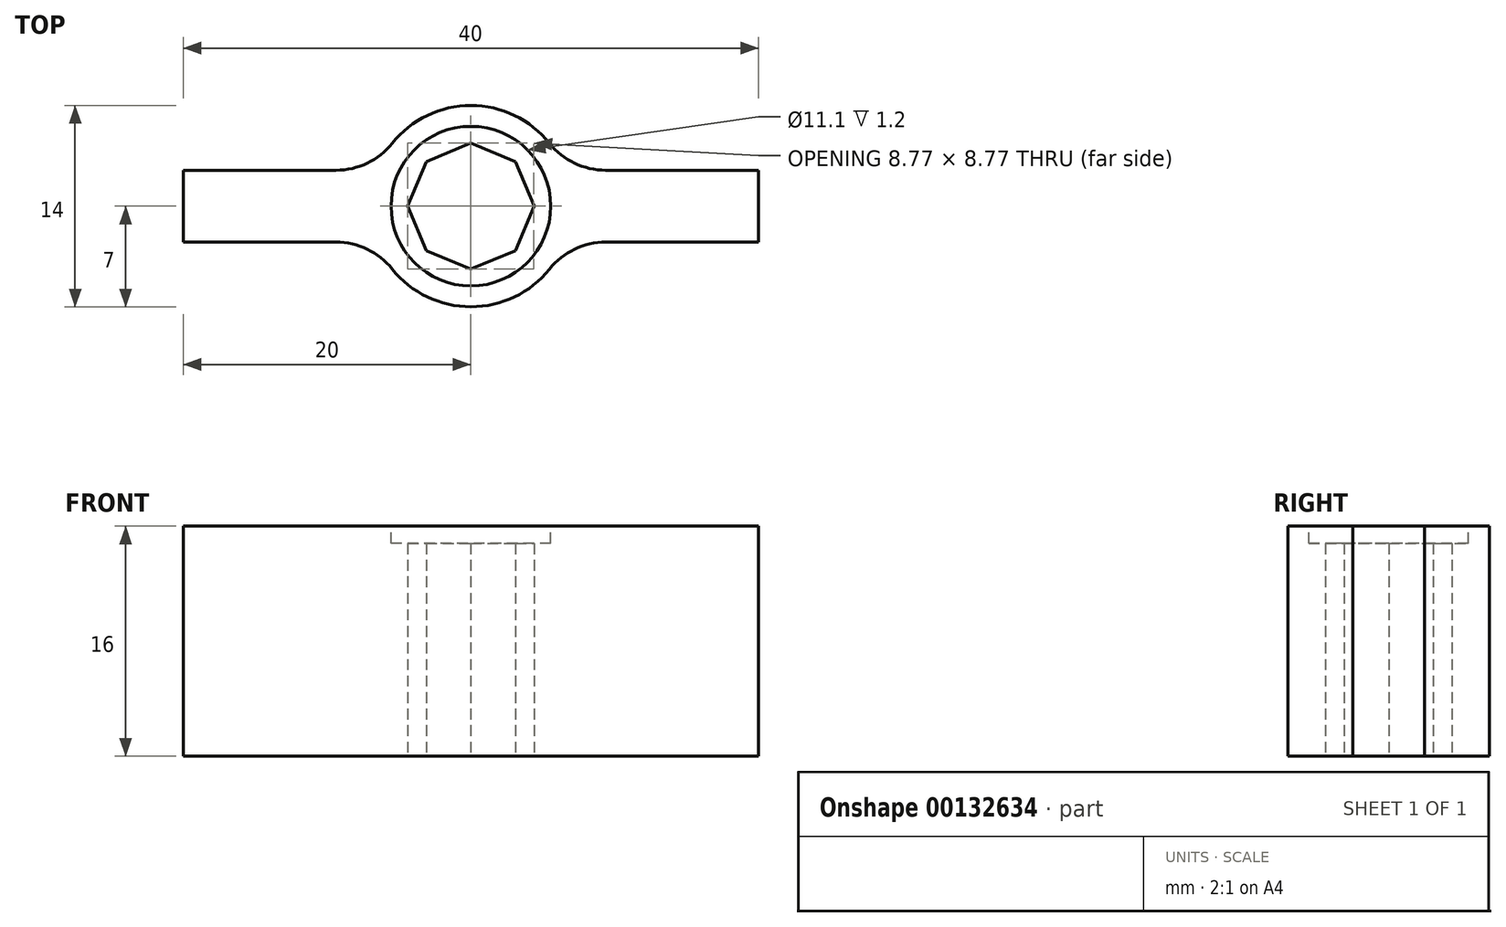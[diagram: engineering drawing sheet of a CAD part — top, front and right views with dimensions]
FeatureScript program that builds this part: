
annotation { "Feature Type Name" : "Feature", "Feature Type Description" : "" }
export const myFeature = defineFeature(function(context is Context, id is Id, definition is map)
    precondition{}
    {
        {
            var Q0;
            Q0=qCreatedBy(makeId("Top.planeOp"),FACE);
            var sketch = newSketch(context, id + "F0", { "sketchPlane" : qUnion([Q0])});
            skCircle(sketch, "E0.cCircle", {"center": v(0, 0) * mm, "radius": 4.05 * mm, "construction": true});
            skLineSegment(sketch, "E0.0", {"start": v(4.38, 0) * mm, "end": v(3.1, -3.1) * mm});
            skLineSegment(sketch, "E0.1", {"start": v(3.1, -3.1) * mm, "end": v(0, -4.38) * mm});
            skLineSegment(sketch, "E0.2", {"start": v(0, -4.38) * mm, "end": v(-3.1, -3.1) * mm});
            skLineSegment(sketch, "E0.3", {"start": v(-3.1, -3.1) * mm, "end": v(-4.38, 0) * mm});
            skLineSegment(sketch, "E0.4", {"start": v(-4.38, 0) * mm, "end": v(-3.1, 3.1) * mm});
            skLineSegment(sketch, "E0.5", {"start": v(-3.1, 3.1) * mm, "end": v(0, 4.38) * mm});
            skLineSegment(sketch, "E0.6", {"start": v(0, 4.38) * mm, "end": v(3.1, 3.1) * mm});
            skLineSegment(sketch, "E0.7", {"start": v(3.1, 3.1) * mm, "end": v(4.38, 0) * mm});
            skPoint(sketch, "E0.0.midPoint", {"position": v(3.74, -1.55) * mm});
            skArc(sketch, "E1", {"start": v(-5.46, -4.37) * mm, "mid": v(0, -7) * mm, "end": v(5.46, -4.37) * mm});
            skLineSegment(sketch, "E2.bottom", {"start": v(20, -2.5) * mm, "end": v(9.37, -2.5) * mm});
            skLineSegment(sketch, "E2.top", {"start": v(20, 2.5) * mm, "end": v(9.37, 2.5) * mm});
            skLineSegment(sketch, "E2.left", {"start": v(20, -2.5) * mm, "end": v(20, 2.5) * mm});
            skLineSegment(sketch, "E2.right", {"start": v(-20, -2.5) * mm, "end": v(-20, 2.5) * mm});
            skLineSegment(sketch, "E3.trimOffspring", {"start": v(-9.37, 2.5) * mm, "end": v(-20, 2.5) * mm});
            skLineSegment(sketch, "E4.trimOffspring", {"start": v(-3.19, 2.5) * mm, "end": v(-3.35, 2.5) * mm});
            skLineSegment(sketch, "E5.trimOffspring", {"start": v(3.35, 2.5) * mm, "end": v(3.19, 2.5) * mm});
            skLineSegment(sketch, "E6.trimOffspring", {"start": v(-3.19, -2.5) * mm, "end": v(-3.35, -2.5) * mm});
            skLineSegment(sketch, "E7.trimOffspring", {"start": v(-9.37, -2.5) * mm, "end": v(-20, -2.5) * mm});
            skArc(sketch, "E8.trimOffspring", {"start": v(5.46, 4.37) * mm, "mid": v(0, 7) * mm, "end": v(-5.46, 4.37) * mm});
            skPoint(sketch, "E9.visualSharp", {"position": v(-6.54, 2.5) * mm});
            skArc(sketch, "E9.filletArc", {"start": v(-9.37, 2.5) * mm, "mid": v(-7.2, 3) * mm, "end": v(-5.46, 4.38) * mm});
            skPoint(sketch, "E10.visualSharp", {"position": v(6.54, 2.5) * mm});
            skArc(sketch, "E10.filletArc", {"start": v(5.46, 4.37) * mm, "mid": v(7.2, 3) * mm, "end": v(9.37, 2.5) * mm});
            skPoint(sketch, "E11.visualSharp", {"position": v(6.54, -2.5) * mm});
            skArc(sketch, "E11.filletArc", {"start": v(9.37, -2.5) * mm, "mid": v(7.2, -3) * mm, "end": v(5.46, -4.37) * mm});
            skPoint(sketch, "E12.visualSharp", {"position": v(-6.54, -2.5) * mm});
            skArc(sketch, "E12.filletArc", {"start": v(-5.46, -4.38) * mm, "mid": v(-7.2, -3) * mm, "end": v(-9.37, -2.5) * mm});
            skSolve(sketch);
        }
        {
            var Q0;
            {var subQ1=sQuery(id+"F0.wireOp",EDGE,"E0.0");Q0=makeQuery(id+"F0.imprint","IMPRINT",FACE,{"disambiguationData":[TD([[makeQuery(id+"F0.imprint","IMPRINT",EDGE,{"derivedFrom":subQ1}),1.0]])]});}
            extrude(context, id + "F1", {"entities" : qUnion([Q0]), "endBound" : BoundingType.SYMMETRIC, "depth" : 16 * mm});
        }
        {
            var Q0;
            Q0=makeQuery(id+"F1.opExtrude","CAP_FACE",FACE,{"disambiguationData":[OSD([sQuery(id+"F0.wireOp",EDGE,"E0.0"),sQuery(id+"F0.wireOp",EDGE,"E0.1"),sQuery(id+"F0.wireOp",EDGE,"E0.2"),sQuery(id+"F0.wireOp",EDGE,"E0.3"),sQuery(id+"F0.wireOp",EDGE,"E0.4"),sQuery(id+"F0.wireOp",EDGE,"E0.5"),sQuery(id+"F0.wireOp",EDGE,"E0.6"),sQuery(id+"F0.wireOp",EDGE,"E0.7"),sQuery(id+"F0.wireOp",EDGE,"E1"),sQuery(id+"F0.wireOp",EDGE,"E2.bottom"),sQuery(id+"F0.wireOp",EDGE,"E2.top"),sQuery(id+"F0.wireOp",EDGE,"E2.left"),sQuery(id+"F0.wireOp",EDGE,"E2.right"),sQuery(id+"F0.wireOp",EDGE,"E3.trimOffspring"),sQuery(id+"F0.wireOp",EDGE,"E7.trimOffspring"),sQuery(id+"F0.wireOp",EDGE,"E8.trimOffspring"),sQuery(id+"F0.wireOp",EDGE,"E9.filletArc"),sQuery(id+"F0.wireOp",EDGE,"E10.filletArc"),sQuery(id+"F0.wireOp",EDGE,"E11.filletArc"),sQuery(id+"F0.wireOp",EDGE,"E12.filletArc")])],"isStart":false});
            var sketch = newSketch(context, id + "F2", { "sketchPlane" : qUnion([Q0])});
            skCircle(sketch, "E13", {"center": v(0, 0) * mm, "radius": 5.55 * mm});
            skSolve(sketch);
        }
        {
            var Q0;
            Q0=makeQuery(id+"F2.imprint","IMPRINT",FACE,{"disambiguationData":[TD([[makeQuery(id+"F2.imprint","IMPRINT",EDGE,{"derivedFrom":sQuery(id+"F2.wireOp",EDGE,"E13")}),1.0]])]});
            extrude(context, id + "F3", {"entities" : qUnion([Q0]), "operationType" : NewBodyOperationType.REMOVE, "oppositeDirection" : true, "depth" : 1.2 * mm});
        }
    });
